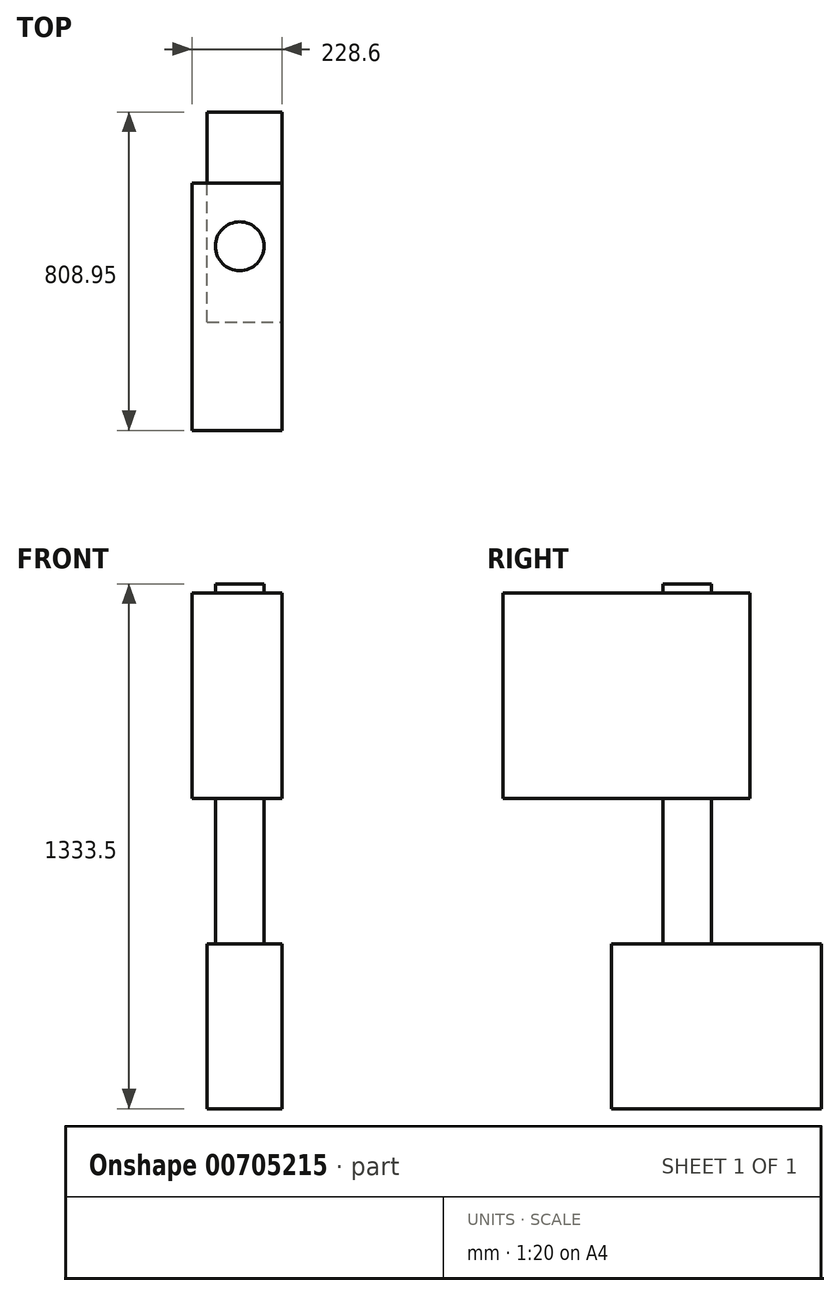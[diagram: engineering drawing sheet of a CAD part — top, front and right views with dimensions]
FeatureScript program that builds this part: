
annotation { "Feature Type Name" : "Feature", "Feature Type Description" : "" }
export const myFeature = defineFeature(function(context is Context, id is Id, definition is map)
    precondition{}
    {
        {
            var Q0;
            Q0=qCreatedBy(makeId("Top.planeOp"),FACE);
            var sketch = newSketch(context, id + "F0", { "sketchPlane" : qUnion([Q0])});
            skLineSegment(sketch, "E0.bottom", {"start": v(0, 0) * mm, "end": v(190.5, 0) * mm});
            skLineSegment(sketch, "E0.top", {"start": v(0, 533.4) * mm, "end": v(190.5, 533.4) * mm});
            skLineSegment(sketch, "E0.left", {"start": v(0, 0) * mm, "end": v(0, 533.4) * mm});
            skLineSegment(sketch, "E0.right", {"start": v(190.5, 0) * mm, "end": v(190.5, 533.4) * mm});
            skSolve(sketch);
        }
        {
            var Q0;
            Q0=makeQuery(id+"F0.imprint","IMPRINT",FACE,{"disambiguationData":[TD([[makeQuery(id+"F0.imprint","IMPRINT",EDGE,{"derivedFrom":sQuery(id+"F0.wireOp",EDGE,"E0.bottom")}),1.0]])]});
            extrude(context, id + "F1", {"entities" : qUnion([Q0]), "depth" : 419.1 * mm, "offsetDistance" : 25.4 * mm});
        }
        {
            var Q0;
            Q0=makeQuery(id+"F1.opExtrude","CAP_FACE",FACE,{"disambiguationData":[OSD([sQuery(id+"F0.wireOp",EDGE,"E0.bottom"),sQuery(id+"F0.wireOp",EDGE,"E0.top"),sQuery(id+"F0.wireOp",EDGE,"E0.left"),sQuery(id+"F0.wireOp",EDGE,"E0.right")])],"isStart":false});
            var sketch = newSketch(context, id + "F2", { "sketchPlane" : qUnion([Q0])});
            skCircle(sketch, "E1", {"center": v(82.93, 192.24) * mm, "radius": 61.95 * mm});
            skSolve(sketch);
        }
        {
            var Q0;
            Q0=makeQuery(id+"F2.imprint","IMPRINT",FACE,{"disambiguationData":[TD([[makeQuery(id+"F2.imprint","IMPRINT",EDGE,{"derivedFrom":sQuery(id+"F2.wireOp",EDGE,"E1")}),1.0]])]});
            extrude(context, id + "F3", {"entities" : qUnion([Q0]), "operationType" : NewBodyOperationType.ADD, "depth" : 914.4 * mm, "offsetDistance" : 25.4 * mm});
        }
        {
            var Q0;
            Q0=makeQuery(id+"F1.opExtrude","SWEPT_FACE",FACE,{"disambiguationData":[OSD([sQuery(id+"F0.wireOp",EDGE,"E0.right")])]});
            var sketch = newSketch(context, id + "F4", { "sketchPlane" : qUnion([Q0])});
            skLineSegment(sketch, "E2.bottom", {"start": v(352.3, 787.7) * mm, "end": v(-275.55, 787.7) * mm});
            skLineSegment(sketch, "E2.top", {"start": v(352.3, 1309.77) * mm, "end": v(-275.55, 1309.77) * mm});
            skLineSegment(sketch, "E2.left", {"start": v(352.3, 787.7) * mm, "end": v(352.3, 1309.77) * mm});
            skLineSegment(sketch, "E2.right", {"start": v(-275.55, 787.7) * mm, "end": v(-275.55, 1309.77) * mm});
            skSolve(sketch);
        }
        {
            var Q0;
            Q0=makeQuery(id+"F4.imprint","IMPRINT",FACE,{"disambiguationData":[TD([[makeQuery(id+"F4.imprint","IMPRINT",EDGE,{"derivedFrom":sQuery(id+"F4.wireOp",EDGE,"E2.bottom")}),-1.0]])]});
            extrude(context, id + "F5", {"entities" : qUnion([Q0]), "operationType" : NewBodyOperationType.ADD, "oppositeDirection" : true, "depth" : 228.6 * mm, "offsetDistance" : 25.4 * mm});
        }
    });
